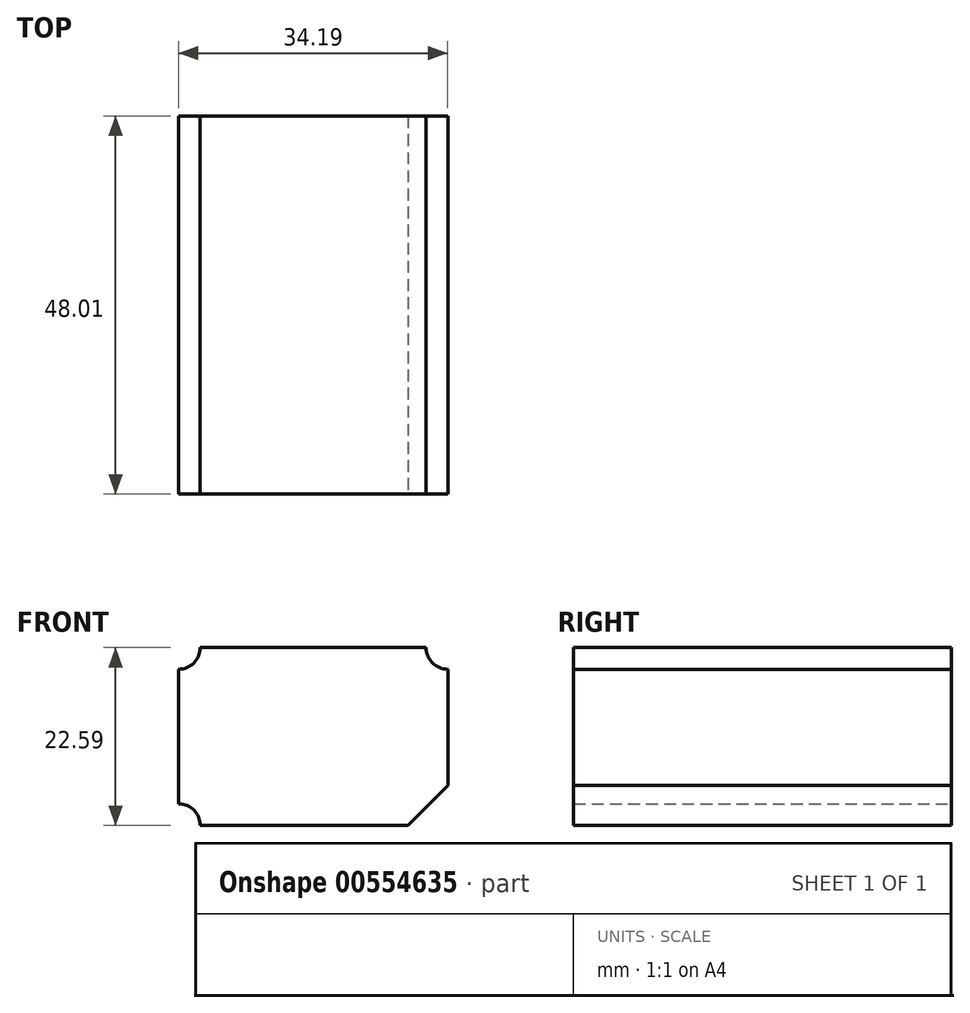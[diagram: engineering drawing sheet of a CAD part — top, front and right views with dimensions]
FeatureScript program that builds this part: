
annotation { "Feature Type Name" : "Feature", "Feature Type Description" : "" }
export const myFeature = defineFeature(function(context is Context, id is Id, definition is map)
    precondition{}
    {
        {
            var Q0;
            Q0=qCreatedBy(makeId("Front.planeOp"),FACE);
            var sketch = newSketch(context, id + "F0", { "sketchPlane" : qUnion([Q0])});
            skLineSegment(sketch, "E0.bottom", {"start": v(55.3, -48.7) * mm, "end": v(21.11, -48.7) * mm});
            skLineSegment(sketch, "E0.top", {"start": v(55.3, -26.1) * mm, "end": v(21.11, -26.1) * mm});
            skLineSegment(sketch, "E0.left", {"start": v(55.3, -48.7) * mm, "end": v(55.3, -26.1) * mm});
            skLineSegment(sketch, "E0.right", {"start": v(21.11, -48.7) * mm, "end": v(21.11, -26.1) * mm});
            skSolve(sketch);
        }
        {
            var Q0;
            Q0=makeQuery(id+"F0.imprint","IMPRINT",FACE,{"disambiguationData":[TD([[makeQuery(id+"F0.imprint","IMPRINT",EDGE,{"derivedFrom":sQuery(id+"F0.wireOp",EDGE,"E0.bottom")}),-1.0]])]});
            extrude(context, id + "F1", {"entities" : qUnion([Q0]), "depth" : 48 * mm, "offsetDistance" : 25.4 * mm});
        }
        {
            var Q0;
            Q0=makeQuery(id+"F1.opExtrude","SWEPT_EDGE",EDGE,{"disambiguationData":[OSD([sQuery(id+"F0.wireOp",EDGE,"E0.bottom"),sQuery(id+"F0.wireOp",EDGE,"E0.left")])]});
            chamfer(context, id + "F2", {"entities" : qUnion([Q0]), "width" : 5.08 * mm, "tangentPropagation" : true});
        }
        {
            var Q0;
            Q0=sQuery(id+"F0.wireOp",VERTEX,"E0.bottom.start");
            var Q1;
            Q1=sQuery(id+"F0.wireOp",VERTEX,"E0.left.end");
            var Q2;
            Q2=sQuery(id+"F0.wireOp",VERTEX,"E0.right.start");
            var Q3;
            Q3=sQuery(id+"F0.wireOp",VERTEX,"E0.right.end");
            var Q4;
            Q4=makeQuery(id+"F1.opExtrude","SWEPT_BODY",BODY,{"disambiguationData":[OSD([sQuery(id+"F0.wireOp",EDGE,"E0.bottom"),sQuery(id+"F0.wireOp",EDGE,"E0.top"),sQuery(id+"F0.wireOp",EDGE,"E0.left"),sQuery(id+"F0.wireOp",EDGE,"E0.right")])]});
            hole(context, id + "F3", {"style" : HoleStyle.SIMPLE, "endStyle" : HoleEndStyle.THROUGH, "oppositeDirection" : true, "standardTappedOrClearance" : lookupTablePath({ "standard" : "ISO", "fit" : "Normal", "size" : "M5", "type" : "Clearance" }), "standardBlindInLast" : lookupTablePath({ "fit" : "Standard", "standard" : "ISO", "size" : "M5", "type" : "Clearance" }), "holeDiameter" : 5.5 * mm, "isTappedThrough" : true, "tappedDepth" : 12.7 * mm, "tapClearance" : 3, "startFromSketch" : true, "locations" : qUnion([Q0, Q1, Q2, Q3]), "scope" : qUnion([Q4])});
        }
    });
